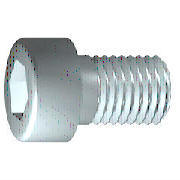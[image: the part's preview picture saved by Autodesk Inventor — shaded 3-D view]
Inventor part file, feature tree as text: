
AUTODESK INVENTOR PART (.ipt)
format: ipt  version: 2015 (Build 190159000, 159)  size: 189,440 bytes
history: native  units: mm (DEFAULTED — no unit token found)
features: sketch x2, extrude x1, plane x1, fillet x1
ambient origin geometry x7: Origin, YZ Plane, XY Plane, X Axis, Y Axis, Z Axis, Center Point
bodies: Solid1 (feature_tree), Body (feature_tree)
feature tree (5):
  extrude  "Slot"  Depth=3.0mm
  plane  "Work Plane1"
  fillet  "Fillet2"  Radius=3.0mm
  sketch  "Sketch1"  dims[d1=14.75mm d2=0.306825mm d3=3.0mm]
  sketch  "Sketch2"  dims[d4=1.3mm d5=60.0deg d6=3.0mm d7=3.0mm d8=2.886751mm d9=5.5mm d10=90.0deg d11=10.0mm d12=0.0mm d13=14.75mm d14=0.0mm d15=0.306725mm d16=0.306725mm d17=0.3mm d19=0.0mm d26=16.0mm d27=45.0deg d28=0.0mm d29=0.0mm d30=0.1mm]
